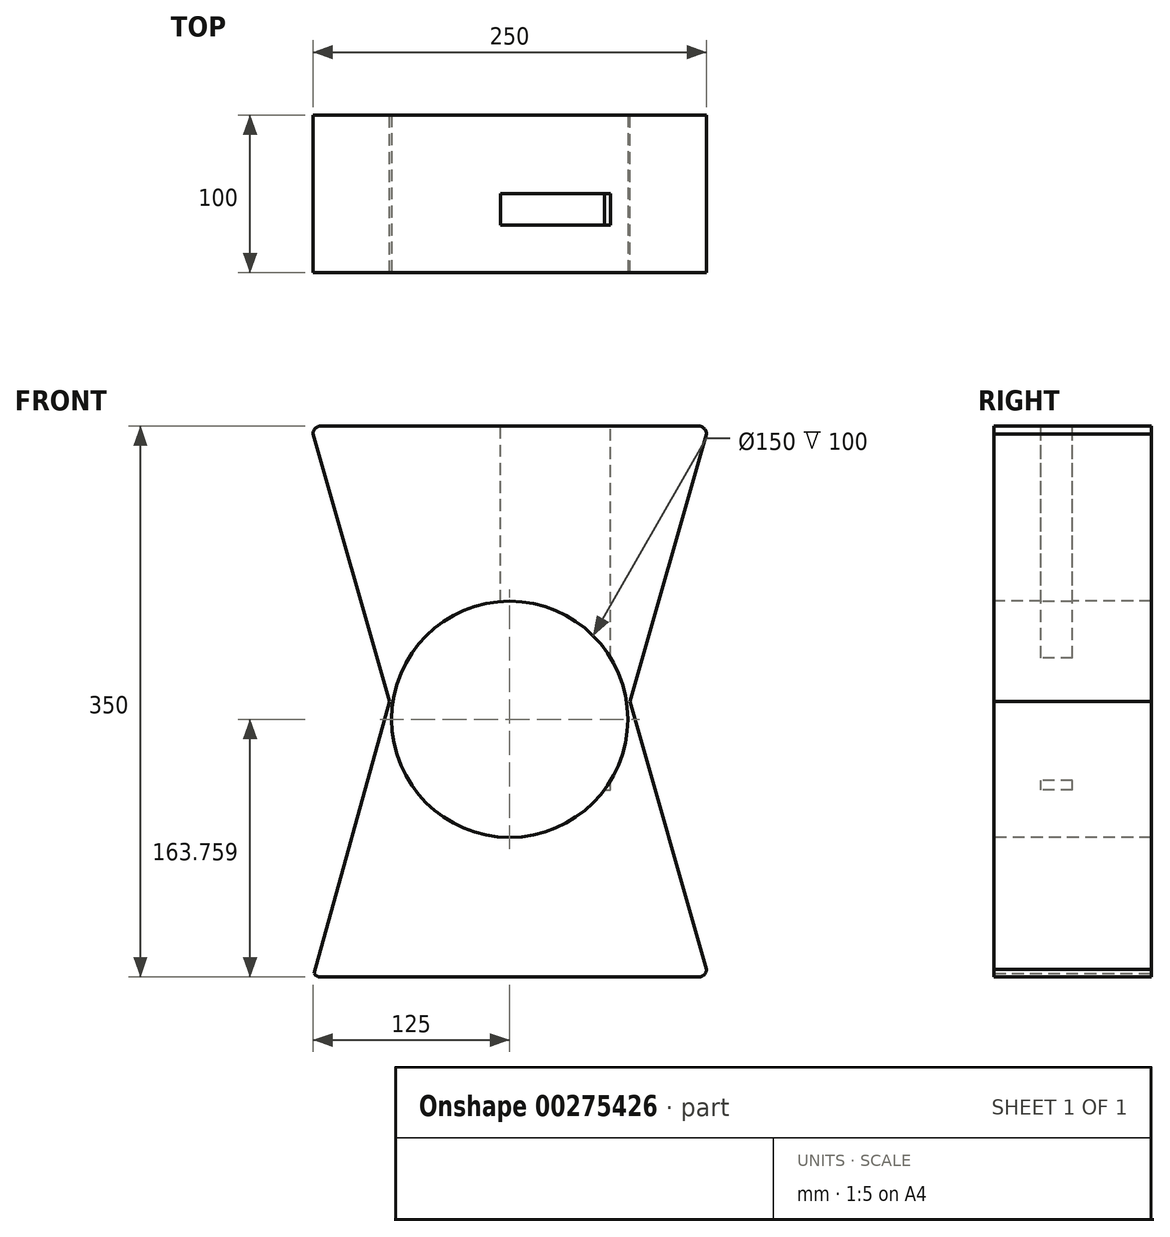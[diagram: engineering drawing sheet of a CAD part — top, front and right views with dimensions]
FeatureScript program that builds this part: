
annotation { "Feature Type Name" : "Feature", "Feature Type Description" : "" }
export const myFeature = defineFeature(function(context is Context, id is Id, definition is map)
    precondition{}
    {
        {
            var Q0;
            Q0=qCreatedBy(makeId("Front.planeOp"),FACE);
            var sketch = newSketch(context, id + "F0", { "sketchPlane" : qUnion([Q0])});
            skLineSegment(sketch, "E0.bottom", {"start": v(-120, 175) * mm, "end": v(120, 175) * mm});
            skLineSegment(sketch, "E0.top", {"start": v(-120, -175) * mm, "end": v(120, -175) * mm});
            skPoint(sketch, "E1.visualSharp", {"position": v(-125, 175) * mm});
            skArc(sketch, "E1.filletArc", {"start": v(-120, 175) * mm, "mid": v(-123.54, 173.54) * mm, "end": v(-125, 170) * mm});
            skPoint(sketch, "E2.visualSharp", {"position": v(-125, -175) * mm});
            skArc(sketch, "E2.filletArc", {"start": v(-125, -170) * mm, "mid": v(-123.54, -173.54) * mm, "end": v(-120, -175) * mm});
            skPoint(sketch, "E3.visualSharp", {"position": v(125, -175) * mm});
            skArc(sketch, "E3.filletArc", {"start": v(120, -175) * mm, "mid": v(123.54, -173.54) * mm, "end": v(125, -170) * mm});
            skPoint(sketch, "E4.visualSharp", {"position": v(125, 175) * mm});
            skArc(sketch, "E4.filletArc", {"start": v(125, 170) * mm, "mid": v(123.54, 173.54) * mm, "end": v(120, 175) * mm});
            skLineSegment(sketch, "E5", {"start": v(125, 170) * mm, "end": v(76.38, 0) * mm});
            skLineSegment(sketch, "E6", {"start": v(76.38, 0) * mm, "end": v(125, -170) * mm});
            skLineSegment(sketch, "E7", {"start": v(-125, 170) * mm, "end": v(-76.38, 0) * mm});
            skLineSegment(sketch, "E8", {"start": v(-76.38, 0) * mm, "end": v(-125, -175) * mm});
            skSolve(sketch);
        }
        {
            var Q0;
            Q0=qSketchRegion(id+"F0",true);
            extrude(context, id + "F1", {"entities" : qUnion([Q0]), "depth" : 100 * mm});
        }
        {
            var Q0;
            Q0=makeQuery(id+"F1.opExtrude","CAP_FACE",FACE,{"disambiguationData":[OSD([sQuery(id+"F0.wireOp",EDGE,"E0.bottom"),sQuery(id+"F0.wireOp",EDGE,"E0.top"),sQuery(id+"F0.wireOp",EDGE,"E0.left"),sQuery(id+"F0.wireOp",EDGE,"E0.right")])],"isStart":false});
            var sketch = newSketch(context, id + "F2", { "sketchPlane" : qUnion([Q0])});
            skCircle(sketch, "E9", {"center": v(0, -11.24) * mm, "radius": 75 * mm});
            skSolve(sketch);
        }
        {
            var Q0;
            Q0=makeQuery(id+"F2.imprint","IMPRINT",FACE,{"disambiguationData":[TD([[makeQuery(id+"F2.imprint","IMPRINT",EDGE,{"derivedFrom":sQuery(id+"F2.wireOp",EDGE,"E9")}),1.0]])]});
            extrude(context, id + "F3", {"entities" : qUnion([Q0]), "operationType" : NewBodyOperationType.REMOVE, "oppositeDirection" : true, "depth" : 267 * mm});
        }
        {
            var Q0;
            Q0=makeQuery(id+"F1.opExtrude","SWEPT_FACE",FACE,{"disambiguationData":[OSD([sQuery(id+"F0.wireOp",EDGE,"E0.bottom")])]});
            var sketch = newSketch(context, id + "F4", { "sketchPlane" : qUnion([Q0])});
            skLineSegment(sketch, "E10.bottom", {"start": v(-5.88, -50) * mm, "end": v(64.12, -50) * mm});
            skLineSegment(sketch, "E10.top", {"start": v(-5.88, -70) * mm, "end": v(64.12, -70) * mm});
            skLineSegment(sketch, "E10.left", {"start": v(-5.88, -50) * mm, "end": v(-5.88, -70) * mm});
            skLineSegment(sketch, "E10.right", {"start": v(64.12, -50) * mm, "end": v(64.12, -70) * mm});
            skSolve(sketch);
        }
        {
            var Q0;
            Q0=qSketchRegion(id+"F4",true);
            extrude(context, id + "F5", {"entities" : qUnion([Q0]), "operationType" : NewBodyOperationType.REMOVE, "oppositeDirection" : true, "depth" : 231 * mm});
        }
    });
